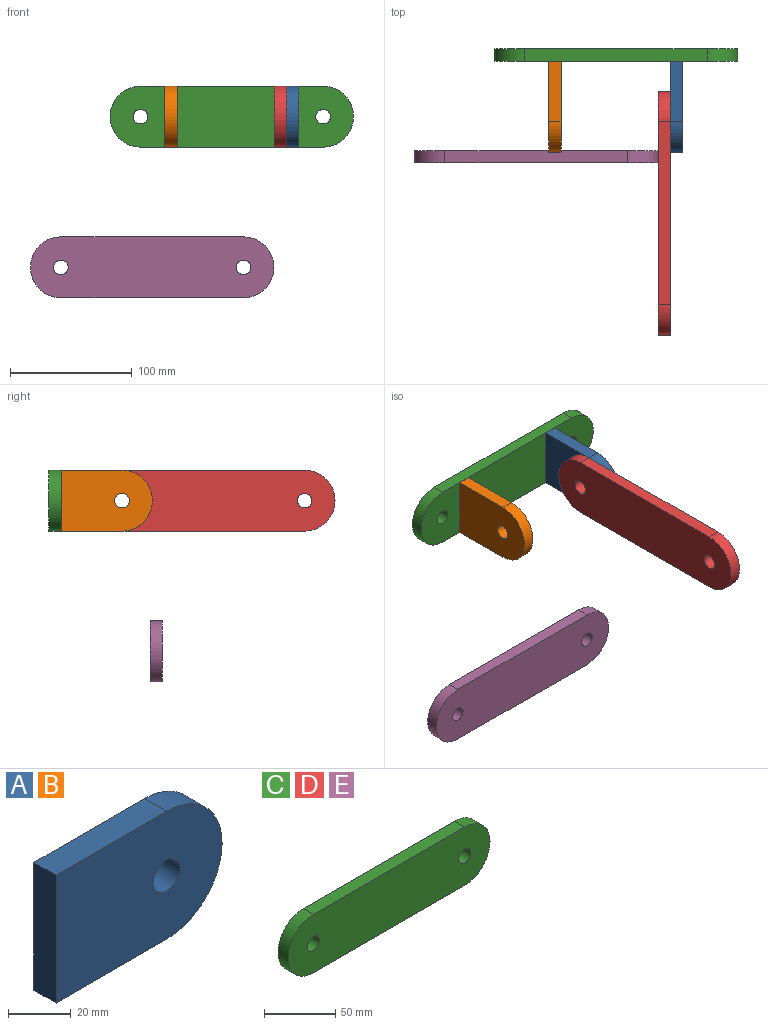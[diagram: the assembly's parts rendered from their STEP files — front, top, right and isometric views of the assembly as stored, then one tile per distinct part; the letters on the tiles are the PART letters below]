
ASSEMBLY  parts=5 mates=3
PART A: 7 faces, bbox 75x10x50 mm
  f0: plane 50x10mm, normal (0,0,1), area 500mm2, adj f1,f4,f5,f6
  f1: plane 50x10mm, normal (-1,0,0), area 500mm2, adj f0,f2,f5,f6
  f2: plane 50x10mm, normal (0,0,-1), area 500mm2, adj f1,f4,f5,f6
  f3: cylinder r=6mm len=12mm, axis (0,1,0), area 377mm2, adj f5,f6
  f4: cylinder r=25mm len=50mm, axis (0,1,0), area 785.4mm2, adj f0,f2,f5,f6
  f5: plane 75x50mm, normal (0,-1,0), area 3368.7mm2, adj f0,f1,f2,f3,f4
  f6: plane 75x50mm, normal (0,1,0), area 3368.7mm2, adj f0,f1,f2,f3,f4
PART B: same geometry as A
PART C: 8 faces, bbox 200x10x50 mm
  f0: plane 150x10mm, normal (0,0,-1), area 1500mm2, adj f1,f5,f6,f7
  f1: cylinder r=25mm len=50mm, axis (0,1,0), area 785.4mm2, adj f0,f2,f6,f7
  f2: plane 150x10mm, normal (0,0,1), area 1500mm2, adj f1,f5,f6,f7
  f3: cylinder r=6mm len=12mm, axis (0,1,0), area 377mm2, adj f6,f7
  f4: cylinder r=6mm len=12mm, axis (0,1,0), area 377mm2, adj f6,f7
  f5: cylinder r=25mm len=50mm, axis (0,1,0), area 785.4mm2, adj f0,f2,f6,f7
  f6: plane 200x50mm, normal (0,-1,0), area 9237.3mm2, adj f0,f1,f2,f3,f4,f5
  f7: plane 200x50mm, normal (0,1,0), area 9237.3mm2, adj f0,f1,f2,f3,f4,f5
PART D: same geometry as C
PART E: same geometry as C
PLACE A rot(axis=(0,0,-1),90deg) t=(12.09,-124.88,19.88)mm
PLACE B rot(axis=(0,0,-1),90deg) t=(-87.91,-124.88,19.88)mm
PLACE C rot(axis=(-0.12,-0.28,-0.95),0deg) t=(34.8,-12.46,-3.26)mm
PLACE D rot(axis=(0,0,1),90deg) t=(-7.91,-69.75,-3.26)mm
PLACE E t=(-30.57,-95.71,-127.01)mm
MATE fastened B.f1 <-> C.f6  axis (0,1,0) through (-92.91,-22.46,66.88)mm
MATE fastened A.f1 <-> C.f6  axis (0,1,0) through (7.09,-22.46,66.88)mm
MATE revolute D.f1 <-> A.f3  axis (1,0,0) through (2.09,-72.46,41.88)mm
